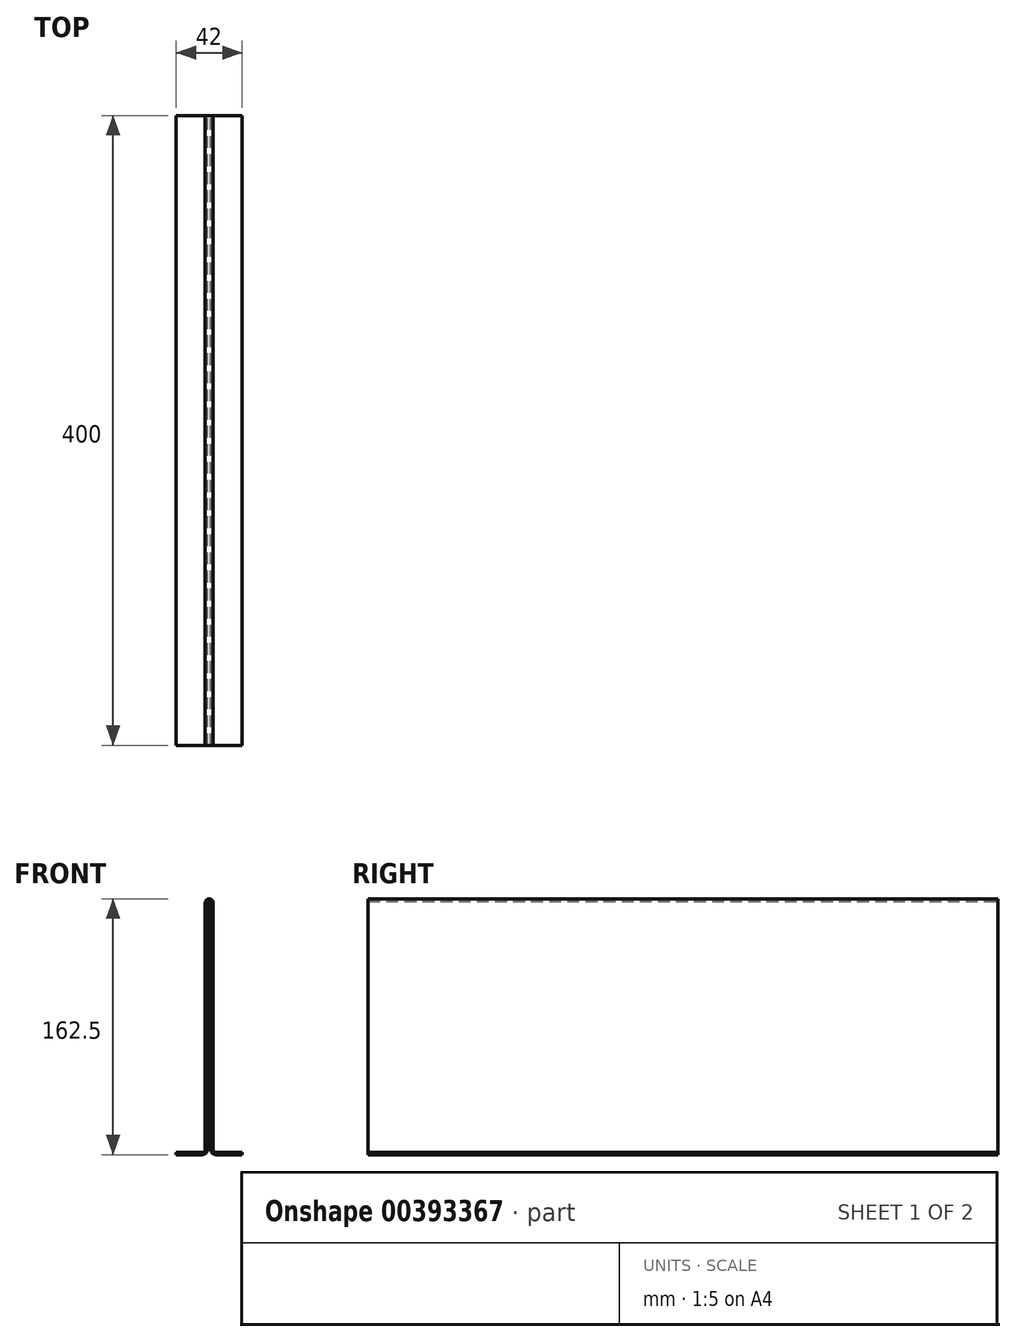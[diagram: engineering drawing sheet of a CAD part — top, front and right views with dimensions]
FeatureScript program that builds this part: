
annotation { "Feature Type Name" : "Feature", "Feature Type Description" : "" }
export const myFeature = defineFeature(function(context is Context, id is Id, definition is map)
    precondition{}
    {
        {
            var Q0;
            Q0=qCreatedBy(makeId("Front.planeOp"),FACE);
            var sketch = newSketch(context, id + "F0", { "sketchPlane" : qUnion([Q0])});
            skArc(sketch, "E0", {"start": v(1, 0) * mm, "mid": v(0.7, 0.7) * mm, "end": v(0, 1) * mm});
            skLineSegment(sketch, "E1", {"start": v(1, 0) * mm, "end": v(1, -156.5) * mm});
            skLineSegment(sketch, "E2", {"start": v(4.5, -160) * mm, "end": v(21, -160) * mm});
            skArc(sketch, "E3", {"start": v(2.5, 0) * mm, "mid": v(1.77, 1.77) * mm, "end": v(0, 2.5) * mm});
            skLineSegment(sketch, "E4", {"start": v(2.5, 0) * mm, "end": v(2.5, -156.5) * mm});
            skLineSegment(sketch, "E5", {"start": v(4.5, -158.5) * mm, "end": v(21, -158.5) * mm});
            skLineSegment(sketch, "E6", {"start": v(21, -158.5) * mm, "end": v(21, -160) * mm});
            skPoint(sketch, "E7.visualSharp", {"position": v(2.5, -158.5) * mm});
            skArc(sketch, "E7.filletArc", {"start": v(2.5, -156.5) * mm, "mid": v(3.09, -157.91) * mm, "end": v(4.5, -158.5) * mm});
            skPoint(sketch, "E8.visualSharp", {"position": v(1, -160) * mm});
            skArc(sketch, "E8.filletArc", {"start": v(1, -156.5) * mm, "mid": v(2.03, -158.97) * mm, "end": v(4.5, -160) * mm});
            skLineSegment(sketch, "E9", {"start": v(0, 8.7) * mm, "end": v(0, -8.74) * mm, "construction": true});
            skLineSegment(sketch, "E10.MirrorCS", {"start": v(-1, 0) * mm, "end": v(-1, -156.5) * mm});
            skLineSegment(sketch, "E11.MirrorCS", {"start": v(-2.5, 0) * mm, "end": v(-2.5, -156.5) * mm});
            skArc(sketch, "E12.MirrorCS", {"start": v(-2.5, 0) * mm, "mid": v(-1.77, 1.77) * mm, "end": v(0, 2.5) * mm});
            skArc(sketch, "E13.MirrorCS", {"start": v(-1, 0) * mm, "mid": v(-0.7, 0.7) * mm, "end": v(0, 1) * mm});
            skLineSegment(sketch, "E14.MirrorCS", {"start": v(-21, -158.5) * mm, "end": v(-21, -160) * mm});
            skArc(sketch, "E15.MirrorCS", {"start": v(-1, -156.5) * mm, "mid": v(-2.03, -158.97) * mm, "end": v(-4.5, -160) * mm});
            skArc(sketch, "E16.MirrorCS", {"start": v(-2.5, -156.5) * mm, "mid": v(-3.09, -157.91) * mm, "end": v(-4.5, -158.5) * mm});
            skLineSegment(sketch, "E17.MirrorCS", {"start": v(-4.5, -160) * mm, "end": v(-21, -160) * mm});
            skPoint(sketch, "E18.MirrorP", {"position": v(-2.5, -158.5) * mm});
            skLineSegment(sketch, "E19.MirrorCS", {"start": v(-4.5, -158.5) * mm, "end": v(-21, -158.5) * mm});
            skPoint(sketch, "E20.MirrorP", {"position": v(-1, -160) * mm});
            skSolve(sketch);
        }
        {
            var Q0;
            Q0 = qSketchRegion(id + "F0", true);
            extrude(context, id + "F1", {"entities" : qUnion([Q0]), "endBound" : BoundingType.SYMMETRIC, "depth" : 400 * mm, "offsetDistance" : 25 * mm});
        }
    });
